# Revit family: Specialty_Equipment-Planter-Planters_Unlimited-Keswick-Rectangular d2-cs1
name_source: partatom
category: Specialty Equipment
units: mm (PartAtom-declared; Revit-internal decimal feet)

## family parameters
Always vertical = Yes
Cut with Voids When Loaded = No
Enable Cutting in Views = Yes
Maintain Annotation Orientation = No
OmniClass Number = 23.40.05.21.17
OmniClass Title = Planters
Part Type = Normal
Room Calculation Point = No
Round Connector Dimension = Use Diameter
Shared = No
Work Plane-Based = No

## types (1)
- Default - Load Type Catalog
    Assembly Code = G2050600
    CD_Height = 18"
    CD_Height Max = 24"
    CD_Height Min = 18"
    CD_Length = 36"
    CD_Length Max = 72"
    CD_Length Min = 36"
    CD_Offset = 0"
    CD_Product Name = Keswick Planter
    CD_Product Page URL = https://www.plantersunlimited.com
    CD_Requested Height = 18"
    CD_Requested Length = 36"
    CD_Requested Width = 18"
    CD_Specification = https://www.plantersunlimited.com
    CD_Width = 18"
    CD_Width Max = 24"
    CD_Width Min = 18"
    Center Divider = No
    Default Elevation = 0"
    Description = Modular Planting Bed
    Manufacturer = Planters Unlimited
    Material = Plastic-Fiberglass-Carlsbad-Semi_Gloss-Charcoal
    Model = Keswick Series Planters
    Type Comments = Rectangular/Square Planter
    URL = https://www.plantersunlimited.com

## geometry (parser evidence)
native form markers: Extrusion x3, Sweep x2
no freeform markers — native parametric forms only
